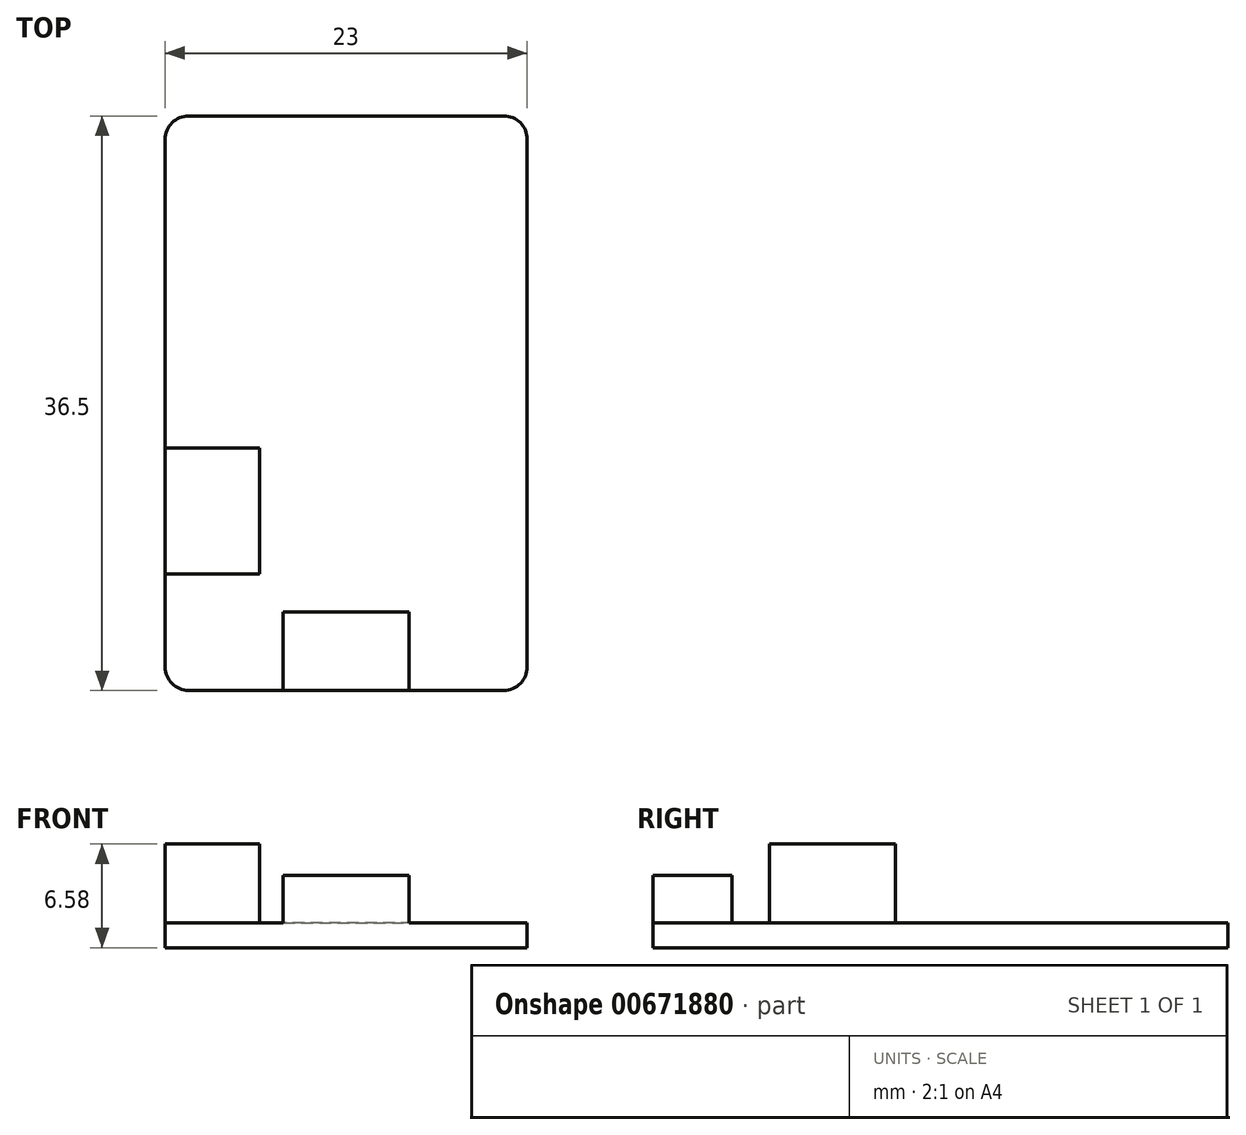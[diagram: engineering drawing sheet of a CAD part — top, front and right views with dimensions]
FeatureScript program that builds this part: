
annotation { "Feature Type Name" : "Feature", "Feature Type Description" : "" }
export const myFeature = defineFeature(function(context is Context, id is Id, definition is map)
    precondition{}
    {
        {
            var Q0;
            Q0=qCreatedBy(makeId("Top.planeOp"),FACE);
            var sketch = newSketch(context, id + "F0", { "sketchPlane" : qUnion([Q0])});
            skLineSegment(sketch, "E0.bottom", {"start": v(11.5, 18.25) * mm, "end": v(-11.5, 18.25) * mm});
            skLineSegment(sketch, "E0.top", {"start": v(11.5, -18.25) * mm, "end": v(-11.5, -18.25) * mm});
            skLineSegment(sketch, "E0.left", {"start": v(11.5, 18.25) * mm, "end": v(11.5, -18.25) * mm});
            skLineSegment(sketch, "E0.right", {"start": v(-11.5, 18.25) * mm, "end": v(-11.5, -18.25) * mm});
            skPoint(sketch, "E0.middle", {"position": v(0, 0) * mm});
            skSolve(sketch);
        }
        {
            var Q0;
            Q0=makeQuery(id+"F0.imprint","IMPRINT",FACE,{"disambiguationData":[TD([[makeQuery(id+"F0.imprint","IMPRINT",EDGE,{"derivedFrom":sQuery(id+"F0.wireOp",EDGE,"E0.bottom")}),1.0]])]});
            extrude(context, id + "F1", {"entities" : qUnion([Q0]), "depth" : 1.58 * mm, "offsetDistance" : 25 * mm});
        }
        {
            var Q0;
            Q0=makeQuery(id+"F1.opExtrude","CAP_FACE",FACE,{"disambiguationData":[OSD([sQuery(id+"F0.wireOp",EDGE,"E0.bottom"),sQuery(id+"F0.wireOp",EDGE,"E0.top"),sQuery(id+"F0.wireOp",EDGE,"E0.left"),sQuery(id+"F0.wireOp",EDGE,"E0.right")])],"isStart":false});
            var sketch = newSketch(context, id + "F2", { "sketchPlane" : qUnion([Q0])});
            skLineSegment(sketch, "E1.bottom", {"start": v(-4, -18.25) * mm, "end": v(4, -18.25) * mm});
            skLineSegment(sketch, "E1.top", {"start": v(-4, -13.25) * mm, "end": v(4, -13.25) * mm});
            skLineSegment(sketch, "E1.left", {"start": v(-4, -18.25) * mm, "end": v(-4, -13.25) * mm});
            skLineSegment(sketch, "E1.right", {"start": v(4, -18.25) * mm, "end": v(4, -13.25) * mm});
            skPoint(sketch, "E1.middle", {"position": v(0, -15.75) * mm});
            skLineSegment(sketch, "E2.bottom", {"start": v(-11.5, -2.85) * mm, "end": v(-5.5, -2.85) * mm});
            skLineSegment(sketch, "E2.top", {"start": v(-11.5, -10.85) * mm, "end": v(-5.5, -10.85) * mm});
            skLineSegment(sketch, "E2.left", {"start": v(-11.5, -2.85) * mm, "end": v(-11.5, -10.85) * mm});
            skLineSegment(sketch, "E2.right", {"start": v(-5.5, -2.85) * mm, "end": v(-5.5, -10.85) * mm});
            skPoint(sketch, "E2.middle", {"position": v(-8.5, -6.85) * mm});
            skSolve(sketch);
        }
        {
            var Q0;
            Q0=makeQuery(id+"F2.imprint","IMPRINT",FACE,{"disambiguationData":[TD([[makeQuery(id+"F2.imprint","IMPRINT",EDGE,{"derivedFrom":sQuery(id+"F2.wireOp",EDGE,"E1.bottom")}),-1.0]])]});
            extrude(context, id + "F3", {"entities" : qUnion([Q0]), "operationType" : NewBodyOperationType.ADD, "depth" : 3 * mm, "offsetDistance" : 25 * mm});
        }
        {
            var Q0;
            Q0=makeQuery(id+"F2.imprint","IMPRINT",FACE,{"disambiguationData":[TD([[makeQuery(id+"F2.imprint","IMPRINT",EDGE,{"derivedFrom":sQuery(id+"F2.wireOp",EDGE,"E2.bottom")}),-1.0]])]});
            extrude(context, id + "F4", {"entities" : qUnion([Q0]), "operationType" : NewBodyOperationType.ADD, "depth" : 5 * mm, "offsetDistance" : 25 * mm});
        }
        {
            var Q0;
            Q0=makeQuery(id+"F1.opExtrude","SWEPT_EDGE",EDGE,{"disambiguationData":[OSD([sQuery(id+"F0.wireOp",EDGE,"E0.top"),sQuery(id+"F0.wireOp",EDGE,"E0.right")])]});
            var Q1;
            Q1=makeQuery(id+"F1.opExtrude","SWEPT_EDGE",EDGE,{"disambiguationData":[OSD([sQuery(id+"F0.wireOp",EDGE,"E0.top"),sQuery(id+"F0.wireOp",EDGE,"E0.left")])]});
            var Q2;
            Q2=makeQuery(id+"F1.opExtrude","SWEPT_EDGE",EDGE,{"disambiguationData":[OSD([sQuery(id+"F0.wireOp",EDGE,"E0.bottom"),sQuery(id+"F0.wireOp",EDGE,"E0.left")])]});
            var Q3;
            Q3=makeQuery(id+"F1.opExtrude","SWEPT_EDGE",EDGE,{"disambiguationData":[OSD([sQuery(id+"F0.wireOp",EDGE,"E0.bottom"),sQuery(id+"F0.wireOp",EDGE,"E0.right")])]});
            fillet(context, id + "F5", {"entities" : qUnion([Q0, Q1, Q2, Q3]), "radius" : 1.5 * mm, "tangentPropagation" : true, "allowEdgeOverflow" : false});
        }
    });
